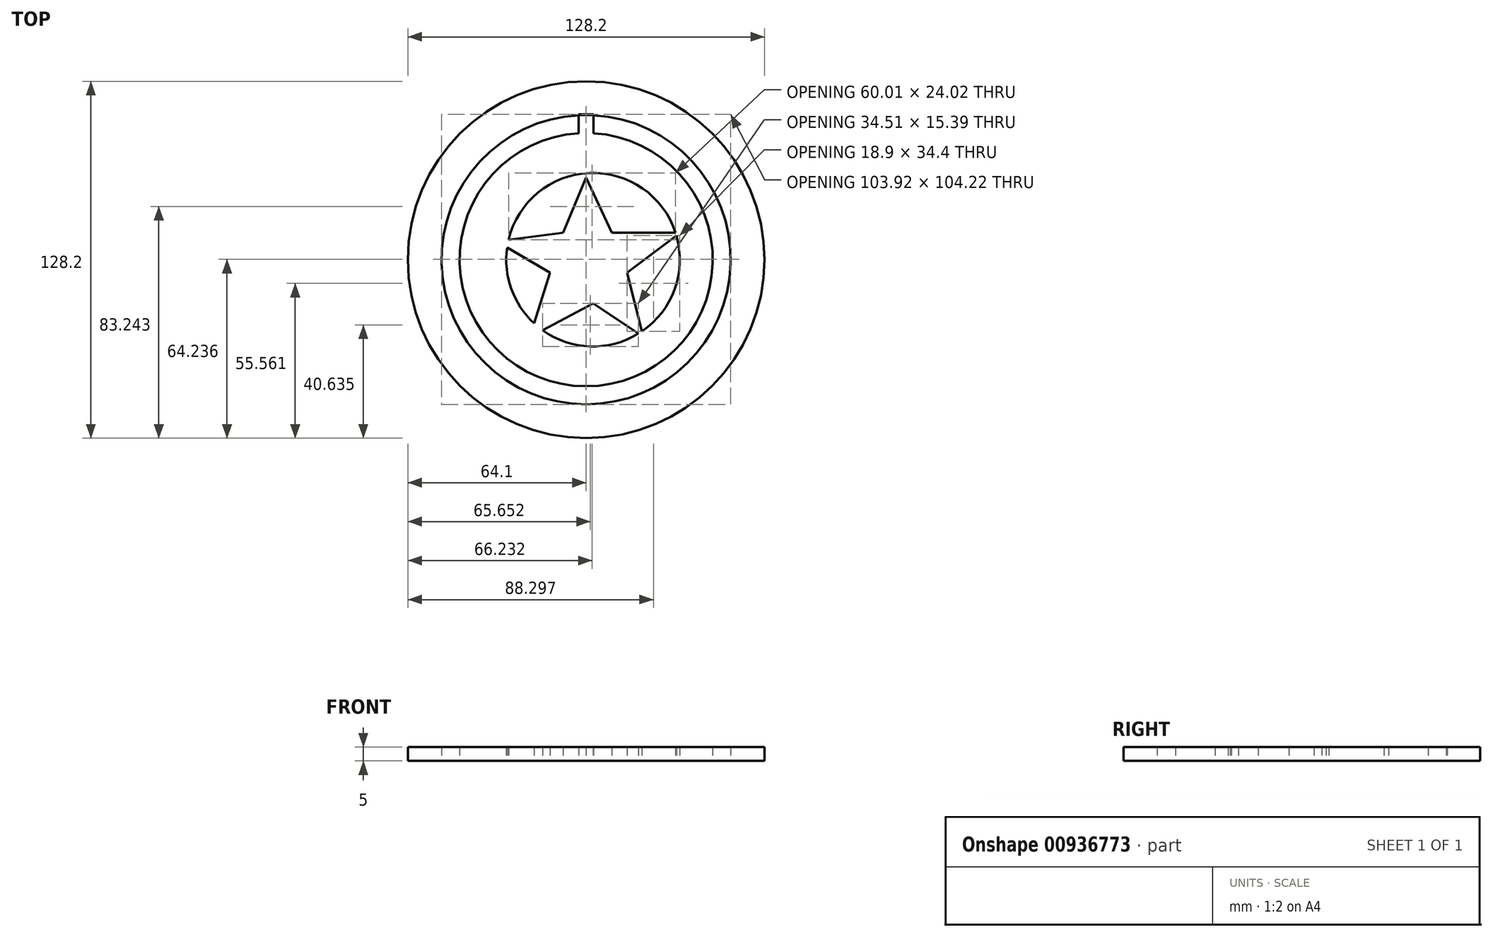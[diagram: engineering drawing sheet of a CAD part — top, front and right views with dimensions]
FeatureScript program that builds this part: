
annotation { "Feature Type Name" : "Feature", "Feature Type Description" : "" }
export const myFeature = defineFeature(function(context is Context, id is Id, definition is map)
    precondition{}
    {
        {
            var Q0;
            Q0=qCreatedBy(makeId("Top.planeOp"),FACE);
            var sketch = newSketch(context, id + "F0", { "sketchPlane" : qUnion([Q0])});
            skLineSegment(sketch, "E0", {"start": v(-32.27, 0) * mm, "end": v(-8.32, 3.07) * mm});
            skLineSegment(sketch, "E1", {"start": v(-8.32, 3.07) * mm, "end": v(0, 22.92) * mm});
            skLineSegment(sketch, "E2", {"start": v(0, 22.92) * mm, "end": v(9.2, 3.07) * mm});
            skLineSegment(sketch, "E3", {"start": v(9.2, 3.07) * mm, "end": v(33.73, 3.07) * mm});
            skLineSegment(sketch, "E4", {"start": v(33.73, 3.07) * mm, "end": v(14.75, -11.24) * mm});
            skLineSegment(sketch, "E5", {"start": v(14.75, -11.24) * mm, "end": v(20.59, -34.31) * mm});
            skLineSegment(sketch, "E6", {"start": v(20.59, -34.31) * mm, "end": v(2.48, -22.34) * mm});
            skLineSegment(sketch, "E7", {"start": v(2.48, -22.34) * mm, "end": v(-20.3, -34.31) * mm});
            skLineSegment(sketch, "E8", {"start": v(-20.3, -34.31) * mm, "end": v(-13, -11.24) * mm});
            skLineSegment(sketch, "E9", {"start": v(-13, -11.24) * mm, "end": v(-32.27, 0) * mm});
            skCircle(sketch, "E10", {"center": v(0, -6.57) * mm, "radius": 64.1 * mm});
            skCircle(sketch, "E11", {"center": v(0, -6.57) * mm, "radius": 51.98 * mm});
            skCircle(sketch, "E12", {"center": v(0, -6.57) * mm, "radius": 45.5 * mm});
            skCircle(sketch, "E13", {"center": v(2.48, -6.57) * mm, "radius": 31.18 * mm});
            skLineSegment(sketch, "E14.bottom", {"start": v(2.65, 38.85) * mm, "end": v(-2.65, 38.85) * mm});
            skLineSegment(sketch, "E14.top", {"start": v(2.65, 45.68) * mm, "end": v(-2.65, 45.68) * mm});
            skLineSegment(sketch, "E14.left", {"start": v(2.65, 38.85) * mm, "end": v(2.65, 45.68) * mm});
            skLineSegment(sketch, "E14.right", {"start": v(-2.65, 38.85) * mm, "end": v(-2.65, 45.68) * mm});
            skPoint(sketch, "E14.middle", {"position": v(0, 42.26) * mm});
            skSolve(sketch);
        }
        {
            var Q0;
            Q0 = qSketchRegion(id + "F0", true);
            var Q1;
            {var subQ0=sQuery(id+"F0.wireOp",EDGE,"E9");var subQ1=sQuery(id+"F0.wireOp",EDGE,"E0");var subQ2=makeQuery(id+"F0.imprint","INTERSECT",VERTEX,{"derivedFrom":[subQ1,subQ0]});Q1=makeQuery(id+"F0.imprint","IMPRINT",FACE,{"disambiguationData":[TD([[makeQuery(id+"F0.imprint","IMPRINT",EDGE,{"disambiguationData":[TD([[subQ2,-1.0]])],"derivedFrom":subQ1}),-1.0]])]});}
            var Q2;
            {var subQ0=sQuery(id+"F0.wireOp",EDGE,"E8");var subQ1=sQuery(id+"F0.wireOp",EDGE,"E7");var subQ2=makeQuery(id+"F0.imprint","INTERSECT",VERTEX,{"derivedFrom":[subQ1,subQ0]});Q2=makeQuery(id+"F0.imprint","IMPRINT",FACE,{"disambiguationData":[TD([[makeQuery(id+"F0.imprint","IMPRINT",EDGE,{"disambiguationData":[TD([[subQ2,1.0]])],"derivedFrom":subQ1}),-1.0]])]});}
            var Q3;
            {var subQ0=sQuery(id+"F0.wireOp",EDGE,"E6");var subQ1=sQuery(id+"F0.wireOp",EDGE,"E5");var subQ2=makeQuery(id+"F0.imprint","INTERSECT",VERTEX,{"derivedFrom":[subQ1,subQ0]});Q3=makeQuery(id+"F0.imprint","IMPRINT",FACE,{"disambiguationData":[TD([[makeQuery(id+"F0.imprint","IMPRINT",EDGE,{"disambiguationData":[TD([[subQ2,1.0]])],"derivedFrom":subQ1}),-1.0]])]});}
            var Q4;
            {var subQ15=sQuery(id+"F0.wireOp",EDGE,"E1");Q4=makeQuery(id+"F0.imprint","IMPRINT",FACE,{"disambiguationData":[TD([[makeQuery(id+"F0.imprint","IMPRINT",EDGE,{"derivedFrom":subQ15}),-1.0]])]});}
            var Q5;
            {var subQ0=sQuery(id+"F0.wireOp",EDGE,"E4");var subQ1=sQuery(id+"F0.wireOp",EDGE,"E3");var subQ2=makeQuery(id+"F0.imprint","INTERSECT",VERTEX,{"derivedFrom":[subQ1,subQ0]});Q5=makeQuery(id+"F0.imprint","IMPRINT",FACE,{"disambiguationData":[TD([[makeQuery(id+"F0.imprint","IMPRINT",EDGE,{"disambiguationData":[TD([[subQ2,1.0]])],"derivedFrom":subQ1}),-1.0]])]});}
            var Q6;
            Q6=makeQuery(id+"F0.imprint","IMPRINT",FACE,{"disambiguationData":[TD([[makeQuery(id+"F0.imprint","IMPRINT",EDGE,{"derivedFrom":sQuery(id+"F0.wireOp",EDGE,"E12")}),1.0]])]});
            var Q7;
            {var subQ14=sQuery(id+"F0.wireOp",EDGE,"E14.bottom");Q7=makeQuery(id+"F0.imprint","IMPRINT",FACE,{"disambiguationData":[TD([[makeQuery(id+"F0.imprint","IMPRINT",EDGE,{"derivedFrom":subQ14}),1.0]])]});}
            var Q8;
            {var subQ0=sQuery(id+"F0.wireOp",EDGE,"E14.left");var subQ1=sQuery(id+"F0.wireOp",EDGE,"E11");var subQ2=makeQuery(id+"F0.imprint","INTERSECT",VERTEX,{"derivedFrom":[subQ1,subQ0]});Q8=makeQuery(id+"F0.imprint","IMPRINT",FACE,{"disambiguationData":[TD([[makeQuery(id+"F0.imprint","IMPRINT",EDGE,{"disambiguationData":[TD([[subQ2,-1.0]])],"derivedFrom":subQ1}),1.0]])]});}
            extrude(context, id + "F1", {"entities" : qUnion([Q0, Q1, Q2, Q3, Q4, Q5, Q6, Q7, Q8]), "depth" : 5 * mm, "offsetDistance" : 25.4 * mm});
        }
    });
